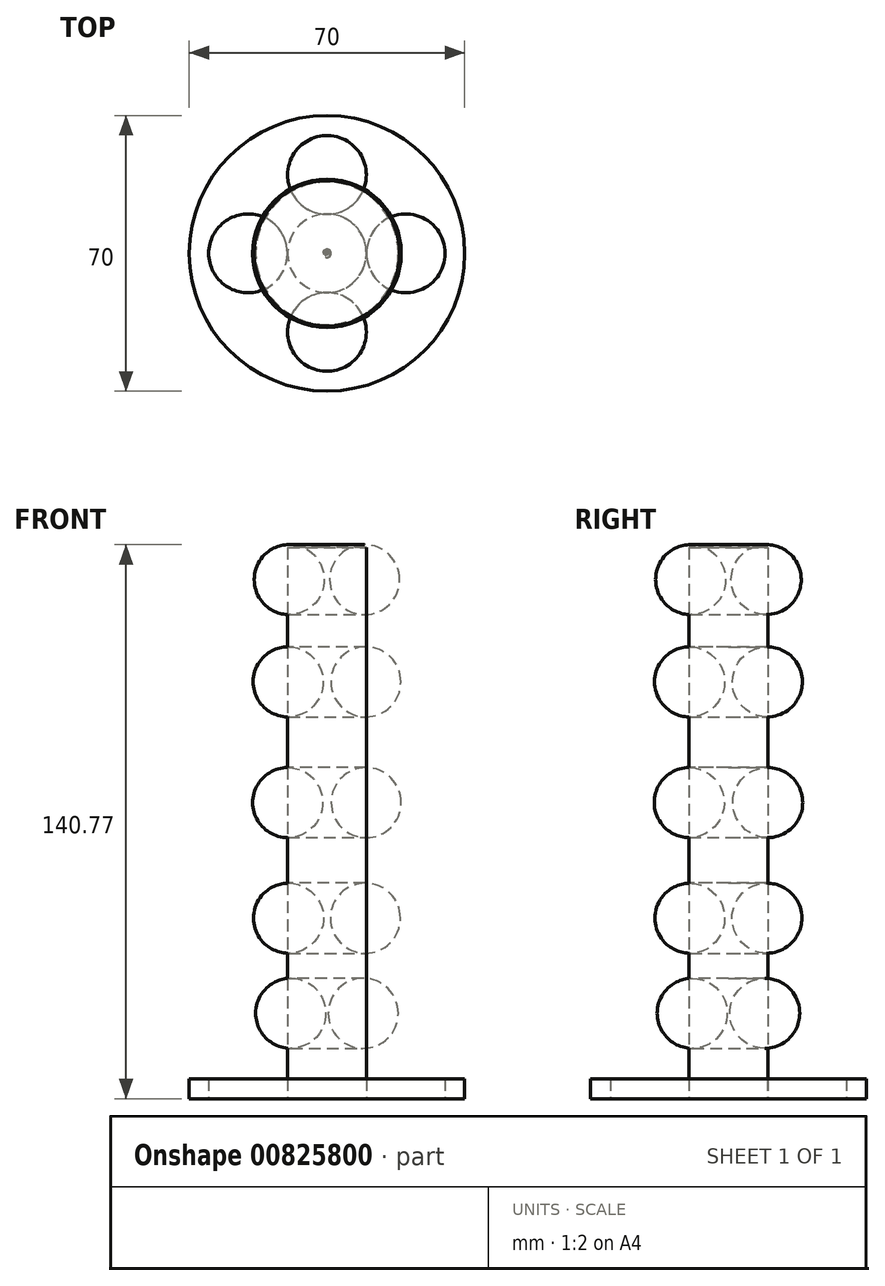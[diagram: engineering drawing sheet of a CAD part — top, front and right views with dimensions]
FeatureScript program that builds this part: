
annotation { "Feature Type Name" : "Feature", "Feature Type Description" : "" }
export const myFeature = defineFeature(function(context is Context, id is Id, definition is map)
    precondition{}
    {
        {
            var Q0;
            Q0=qCreatedBy(makeId("Top.planeOp"),FACE);
            var sketch = newSketch(context, id + "F0", { "sketchPlane" : qUnion([Q0])});
            skCircle(sketch, "E0", {"center": v(0, 0) * mm, "radius": 10 * mm});
            skSolve(sketch);
        }
        {
            var Q0;
            Q0=makeQuery(id+"F0.imprint","IMPRINT",FACE,{"disambiguationData":[TD([[makeQuery(id+"F0.imprint","IMPRINT",EDGE,{"derivedFrom":sQuery(id+"F0.wireOp",EDGE,"E0")}),1.0]])]});
            extrude(context, id + "F1", {"entities" : qUnion([Q0]), "depth" : 140 * mm, "offsetDistance" : 25 * mm});
        }
        {
            var Q0;
            Q0=qCreatedBy(makeId("Top.planeOp"),FACE);
            var sketch = newSketch(context, id + "F2", { "sketchPlane" : qUnion([Q0])});
            skCircle(sketch, "E1", {"center": v(0, 0) * mm, "radius": 35 * mm});
            skSolve(sketch);
        }
        {
            var Q0;
            Q0=makeQuery(id+"F2.imprint","IMPRINT",FACE,{"disambiguationData":[TD([[makeQuery(id+"F2.imprint","IMPRINT",EDGE,{"derivedFrom":sQuery(id+"F2.wireOp",EDGE,"E1")}),1.0]])]});
            extrude(context, id + "F3", {"entities" : qUnion([Q0]), "operationType" : NewBodyOperationType.ADD, "depth" : 5 * mm, "offsetDistance" : 25 * mm});
        }
        {
            var Q0;
            Q0=makeQuery(id+"F3.boolean.opBoolean","MERGE",FACE,{"derivedFrom":[makeQuery(id+"F1.opExtrude","CAP_FACE",FACE,{"disambiguationData":[OSD([sQuery(id+"F0.wireOp",EDGE,"E0")])],"isStart":true}),makeQuery(id+"F3.opExtrude","CAP_FACE",FACE,{"disambiguationData":[OSD([sQuery(id+"F2.wireOp",EDGE,"E1")])],"isStart":true})]});
            var sketch = newSketch(context, id + "F4", { "sketchPlane" : qUnion([Q0])});
            skCircle(sketch, "E2", {"center": v(0, 0) * mm, "radius": 20 * mm});
            skSolve(sketch);
        }
        {
            var Q0;
            Q0=makeQuery(id+"F4.imprint","IMPRINT",FACE,{"disambiguationData":[TD([[makeQuery(id+"F4.imprint","IMPRINT",EDGE,{"derivedFrom":sQuery(id+"F4.wireOp",EDGE,"E2")}),-1.0]])]});
            var sketch = newSketch(context, id + "F5", { "sketchPlane" : qUnion([Q0])});
            skCircle(sketch, "E3", {"center": v(0, 19.98) * mm, "radius": 10 * mm});
            skCircle(sketch, "E4", {"center": v(20.05, 0) * mm, "radius": 10 * mm});
            skCircle(sketch, "E5", {"center": v(0, -19.93) * mm, "radius": 10 * mm});
            skCircle(sketch, "E6", {"center": v(-20.04, 0) * mm, "radius": 10 * mm});
            skSolve(sketch);
        }
        {
            var Q0;
            Q0 = qSketchRegion(id + "F5", true);
            extrude(context, id + "F6", {"entities" : qUnion([Q0]), "operationType" : NewBodyOperationType.REMOVE, "oppositeDirection" : true, "depth" : 5 * mm, "offsetDistance" : 25 * mm});
        }
        {
            var Q0;
            Q0=qCreatedBy(makeId("Front.planeOp"),FACE);
            var sketch = newSketch(context, id + "F7", { "sketchPlane" : qUnion([Q0])});
            skCircle(sketch, "E7", {"center": v(9.88, 105.9) * mm, "radius": 8.9 * mm});
            skCircle(sketch, "E8", {"center": v(9.97, 75.22) * mm, "radius": 8.9 * mm});
            skCircle(sketch, "E9", {"center": v(9.77, 45.85) * mm, "radius": 8.9 * mm});
            skCircle(sketch, "E10", {"center": v(9.59, 131.88) * mm, "radius": 8.9 * mm});
            skCircle(sketch, "E11", {"center": v(9.21, 21.7) * mm, "radius": 8.9 * mm});
            skSolve(sketch);
        }
        {
            var Q0;
            Q0=makeQuery(id+"F7.imprint","IMPRINT",FACE,{"disambiguationData":[TD([[makeQuery(id+"F7.imprint","IMPRINT",EDGE,{"derivedFrom":sQuery(id+"F7.wireOp",EDGE,"E7")}),1.0]])]});
            var Q1;
            Q1=makeQuery(id+"F7.imprint","IMPRINT",FACE,{"disambiguationData":[TD([[makeQuery(id+"F7.imprint","IMPRINT",EDGE,{"derivedFrom":sQuery(id+"F7.wireOp",EDGE,"E8")}),1.0]])]});
            var Q2;
            Q2=makeQuery(id+"F7.imprint","IMPRINT",FACE,{"disambiguationData":[TD([[makeQuery(id+"F7.imprint","IMPRINT",EDGE,{"derivedFrom":sQuery(id+"F7.wireOp",EDGE,"E9")}),1.0]])]});
            var Q3;
            Q3=makeQuery(id+"F7.imprint","IMPRINT",FACE,{"disambiguationData":[TD([[makeQuery(id+"F7.imprint","IMPRINT",EDGE,{"derivedFrom":sQuery(id+"F7.wireOp",EDGE,"E11")}),1.0]])]});
            var Q4;
            Q4=makeQuery(id+"F7.imprint","IMPRINT",FACE,{"disambiguationData":[TD([[makeQuery(id+"F7.imprint","IMPRINT",EDGE,{"derivedFrom":sQuery(id+"F7.wireOp",EDGE,"E10")}),1.0]])]});
            var Q5;
            Q5=makeQuery(id+"F1.opExtrude","SWEPT_FACE",FACE,{"disambiguationData":[OSD([sQuery(id+"F0.wireOp",EDGE,"E0")])]});
            revolve(context, id + "F8", {"surfaceOperationType" : NewSurfaceOperationType.NEW, "entities" : qUnion([Q0, Q1, Q2, Q3, Q4]), "axis" : qUnion([Q5]), "revolveType" : RevolveType.FULL});
        }
    });
